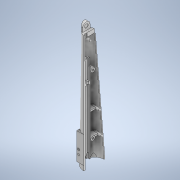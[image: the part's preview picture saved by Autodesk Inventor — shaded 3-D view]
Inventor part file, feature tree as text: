
AUTODESK INVENTOR PART (.ipt)
format: ipt  version: 2021 (Build 250183000, 183)  size: 1,114,112 bytes
history: native  units: mm
features: sketch x40, extrude x37, plane x17, fillet x7, hole x3, thread x3, loft x2, revolve x2, other x1
ambient origin geometry x8: Origin, YZ Plane, XZ Plane, XY Plane, X Axis, Y Axis, Z Axis, Center Point
bodies: Body1 (feature_tree)
feature tree (112):
  other  "Sólido1"
  plane  "Plano de trabajo1"
  plane  "Plano de trabajo2"
  plane  "Plano de trabajo4"
  plane  "Plano de trabajo5"
  plane  "Plano de trabajo6"
  sketch  "Boceto1"  dims[d1=250.0mm d2=0.0mm d3=-80.0mm d4=-110.0mm]
  sketch  "Boceto2"  dims[d5=-140.0mm d7=-0.0mm d8=2.0mm]
  sketch  "Boceto3"  dims[d9=140.0mm d10=250.0mm]
  sketch  "Boceto4"  dims[d11=24.0mm d22=0.0mm d23=90.0deg d24=0.0mm d25=90.0deg]
  sketch  "Boceto6"  dims[d44=45.0mm d49=29.11157mm]
  sketch  "Boceto7"  dims[d50=29.11157mm d53=29.11157mm]
  loft  "Solevación1"
  fillet  "Empalme2"  [1 undecoded]
  extrude  "Extrusión1"  TaperAngle=0.0deg  [1 undecoded]
  fillet  "Empalme5"  Radius=2.0mm
  plane  "Plano de trabajo7"
  extrude  "Extrusión2"  Depth=250.0mm
  plane  "Plano de trabajo8"
  plane  "Plano de trabajo9"
  loft  "Solevación9"
  plane  "Plano de trabajo10"
  extrude  "Extrusión3"  Depth=29.11157mm
  plane  "Plano de trabajo11"
  revolve  "Revolución1"  [1 undecoded]
  revolve  "Revolución2"  [1 undecoded]
  extrude  "Extrusión4"  Depth=32.5mm
  plane  "Plano de trabajo12"
  extrude  "Extrusión5"  Depth=44.747934mm
  plane  "Plano de trabajo13"
  plane  "Plano de trabajo14"
  extrude  "Extrusión6"  Depth=42.747934mm
  extrude  "Extrusión7"  Depth=42.747934mm
  extrude  "Extrusión8"  Depth=13.0mm
  extrude  "Extrusión11"  Depth=7.75mm
  extrude  "Extrusión9"  Depth=7.75mm
  extrude  "Extrusión10"  Depth=16.0mm
  extrude  "Extrusión12"  Depth=12.0mm
  sketch  "Boceto30"  dims[d160=-19.75mm d161=0.0mm]
  extrude  "Extrusión13"  Depth=7.75mm
  extrude  "Extrusión14"  Depth=7.75mm
  extrude  "Extrusión15"  TaperAngle=0.0deg  [1 undecoded]
  hole  "Agujero1"  [1 undecoded]
  thread  "Rosca1"  [1 undecoded]
  extrude  "Extrusión16"  Depth=2.0mm
  plane  "Plano de trabajo16"
  extrude  "Extrusión17"  TaperAngle=0.0deg  [1 undecoded]
  extrude  "Extrusión18"  TaperAngle=0.0deg  [1 undecoded]
  plane  "Plano de trabajo17"
  sketch  "Boceto46"  dims[d185=2.0mm d187=1.0mm]
  hole  "Agujero2"  [1 undecoded]
  hole  "Agujero3"  [1 undecoded]
  plane  "Plano de trabajo19"
  sketch  "Boceto50"  dims[d193=0.25mm d194=90.0deg d196=4.381635mm d197=0.0mm]
  extrude  "Extrusión22"  Depth=12.0mm
  extrude  "Extrusión23"  [1 undecoded]
  extrude  "Extrusión24"  Depth=0.75mm
  plane  "Plano de trabajo20"
  extrude  "Extrusión25"  Depth=1.0mm
  fillet  "Empalme6"  Radius=11.0mm
  fillet  "Empalme7"  Radius=17.453293mm
  sketch  "Boceto49"  dims[d191=2.0mm d192=0.25mm]
  extrude  "Extrusión29"  Depth=0.75mm
  extrude  "Extrusión30"  Depth=0.25mm
  sketch  "Boceto44"  dims[d181=0.75mm d182=0.25mm]
  sketch  "Boceto47"  dims[d189=3.0mm d190=2.0mm]
  extrude  "Extrusión26"  Depth=0.25mm
  extrude  "Extrusión27"  Depth=1.0mm
  extrude  "Extrusión28"  Depth=2.0mm
  sketch  "Boceto45"  dims[d183=1.0mm d184=0.25mm]
  extrude  "Extrusión31"  Depth=0.25mm
  extrude  "Extrusión32"  TaperAngle=90.0deg  [1 undecoded]
  fillet  "Empalme8"  Radius=4.381635mm
  extrude  "Extrusión33"  Depth=12.0mm
  extrude  "Extrusión34"  Depth=9.0mm
  thread  "Rosca2"  [1 undecoded]
  thread  "Rosca3"  [1 undecoded]
  fillet  "Empalme9"  Radius=201.65mm
  extrude  "Extrusión35"  Depth=0.5mm
  extrude  "Extrusión36"  [1 undecoded]
  sketch  "Boceto53"  dims[d205=0.0mm d206=0.5mm]
  extrude  "Agujero_tornillo_caja"  Depth=100.0mm TaperAngle=0.0deg
  extrude  "Extrusión39"  Depth=35.0mm TaperAngle=0.0deg
  extrude  "Test_section"  Depth=210.0mm TaperAngle=0.0deg
  extrude  "Agujero_cables"  Depth=2.0mm
  fillet  "Empalme10"  Radius=1.059493mm
  sketch  "Boceto9"  dims[d59=29.11157mm d61=29.11157mm]
  sketch  "Boceto10"  dims[d65=22.5mm d66=32.5mm]
  sketch  "Boceto15"  dims[d67=22.5mm d90=44.747934mm]
  sketch  "Boceto16"  dims[d91=42.747934mm d93=42.747934mm]
  sketch  "Boceto17"  dims[d96=0.0mm d97=90.0deg d98=0.0mm d99=90.0deg d100=0.0mm d101=90.0deg d102=0.0mm d103=90.0deg d112=42.747934mm]
  sketch  "Boceto18"  dims[d115=5.0mm d120=13.0mm]
  sketch  "Boceto19"  dims[d121=6.5mm d124=7.75mm]
  sketch  "Boceto20"  dims[d125=7.75mm d126=7.75mm]
  sketch  "Boceto21"  dims[d127=7.75mm d130=16.0mm]
  sketch  "Boceto22"  dims[d131=0.0mm d132=12.0mm]
  sketch  "Boceto24"  dims[d133=12.0mm d134=7.75mm]
  sketch  "Boceto25"  dims[d135=6.5mm d136=7.75mm]
  sketch  "Boceto26"  dims[d137=15.0mm d138=0.0mm]
  sketch  "Boceto27"  dims[d146=-8.5mm d147=30.0mm d148=2.0mm]
  sketch  "Boceto28"  dims[d149=25.12mm d150=2.0mm]
  sketch  "Boceto29"  dims[d151=10.357mm d156=0.0mm d157=90.0deg d158=0.0mm d159=90.0deg]
  sketch  "Boceto31"  dims[d163=0.0mm d164=2.0mm]
  sketch  "Boceto36"  dims[d165=15.0mm d166=4.0mm]
  sketch  "Boceto37"  dims[d167=30.0mm d168=12.0mm]
  sketch  "Boceto38"  dims[d169=0.0mm d170=-7.25mm]
  sketch  "Boceto39"  dims[d171=4.5mm d172=0.75mm]
  sketch  "Boceto40"  dims[d173=2.5mm d174=1.0mm d176=11.0mm d177=17.453293mm]
  sketch  "Boceto41"  dims[d179=2.939597mm d180=0.75mm]
  sketch  "Boceto51"  dims[d198=-48.35mm d199=12.0mm]
  sketch  "Boceto52"  dims[d200=20.0mm d201=9.0mm d202=9.0mm d203=2.0mm d204=201.65mm]
  sketch  "Boceto54"  dims[d207=0.25mm d208=-7.5mm d209=100.0mm d210=0.0mm d211=35.0mm d212=0.0mm d213=210.0mm d214=0.0mm d215=2.0mm d216=1.059493mm d217=6.5mm d218=1.059493mm d219=5.0mm d220=2.0mm d221=0.0mm d222=2.0mm d223=6.5mm d224=1.059493mm d225=5.0mm d226=4.85mm d227=2.0mm d228=0.0mm d229=6.0mm d230=10.0mm d231=3.0mm d232=11.0mm d233=10.5mm d235=30.0deg d236=4.75mm d237=0.0mm d238=-17.0mm d239=100.0mm d240=0.0mm d241=6.5mm d242=1.65mm d243=3.3mm d244=15.6mm d245=2.0mm d247=16.0mm d248=2.0mm d249=0.0mm d250=4.5mm d251=0.75mm d252=2.5mm d253=1.0mm d254=11.0mm d255=17.453293mm d256=2.939597mm d257=0.75mm d258=0.75mm d259=0.25mm d260=1.0mm d261=0.25mm d262=2.0mm d263=1.0mm d264=3.0mm d265=2.0mm d266=2.0mm d267=0.25mm d268=0.25mm d269=40.0mm d270=1.0mm d271=1.0mm d272=7.75mm d273=0.5mm d274=8.5mm d275=90.0deg d276=0.0mm d277=17.75mm d280=22.5mm d281=2.0mm d282=0.0mm d283=0.0mm d292=2.0mm d293=0.0mm d296=3.5mm d297=0.0mm d299=4.0mm d300=3.708mm d301=3.023mm d302=2.0mm d303=14.3117mm d304=16.0mm d305=0.0mm d306=16.0mm d307=0.0mm d314=6.0mm d315=19.2mm d316=6.0mm d317=19.2mm d318=13.0mm d320=6.0mm d321=19.2mm d322=13.0mm d323=6.0mm d324=19.2mm d325=13.0mm d326=7.0mm d332=10.0mm d333=0.0mm d335=-41.6mm d336=4.0mm d337=1.0mm d338=9.0mm d339=4.0mm d340=1.0mm d341=9.0mm d342=4.0mm d343=5.2mm d344=6.0mm d345=0.0mm d346=15.0mm d347=5.0mm d349=5.0mm d351=0.0mm d352=45.0mm d354=10.0mm d355=10.0mm d356=0.0mm d357=15.0mm d358=0.0mm d359=2.0mm d363=50.4125mm d376=14.059493mm d377=2.0mm d378=0.0mm d379=2.0mm d380=11.25mm d381=90.0mm d382=290.0mm d383=14.059493mm d384=100.825mm d390=30.940507mm d391=2.0mm d392=100.825mm d393=14.790546mm d394=2.0mm d395=3.0mm d396=4.0mm d397=4.0mm d398=4.0mm d399=4.0mm d400=8.128453mm d401=12.0mm d402=4.45mm d403=2.5mm d404=1.65mm d405=1.65mm d406=1.0mm d407=2.0mm d408=2.0mm d409=0.0mm d411=50.4125mm d412=4.0mm d418=13.059493mm d419=6.5mm d420=6.5mm d421=50.4125mm d422=126.03125mm d423=0.0mm d424=15.0mm d425=5.0mm d426=5.0mm d427=0.0mm d428=45.0mm d429=10.0mm d430=2.0mm d431=4.0mm d432=6.0mm d433=8.0mm d434=2.0mm d435=90.0deg d436=20.0mm d437=0.0mm d438=4.0mm d439=6.0mm d440=8.0mm d441=2.0mm d442=90.0deg d443=20.0mm d444=0.0mm d446=10.0mm d447=2.0mm d448=11.5mm d450=4.0mm d451=4.0mm d452=90.0mm d453=750.0mm d454=22.5mm d455=43.0mm d456=44.0mm d457=14.059493mm d458=11.25mm d461=22.5mm d462=43.0mm d463=7.059493mm d464=3.0mm d465=6.0mm d466=3.0mm d467=6.0mm d468=45.0mm d469=67.0mm d470=19.686mm d471=30.0mm d472=15.0mm d473=0.0mm d474=1.5mm d475=2.0mm d476=1.5mm d477=2.0mm d478=57.0mm d479=0.0mm d480=57.0mm d481=0.0mm d482=53.0mm d483=0.0mm d484=37.0mm d485=0.0mm d486=-1.5mm d487=33.895511mm d488=2.6mm d489=60.0deg d490=45.0deg d491=15.0mm d492=1.6mm d493=0.0mm d494=180.0mm d495=0.0mm d496=180.0mm d497=0.0mm d498=2.0mm d499=0.0mm d500=4.4mm d501=4.1mm d502=10.0mm d503=0.0mm d504=7.0mm d505=0.0mm d506=9.0mm d507=9.0mm d508=0.0mm d509=0.0mm d510=6.0mm d511=0.0mm d512=2.0mm d513=0.0mm d514=0.0mm d515=10.0mm d516=0.0mm d517=10.0mm d518=0.0mm d519=10.0mm d520=0.0mm d521=1.0mm d522=1.0mm d523=6.5mm d524=9.0mm d525=3.0mm d526=1.5mm d527=3.0mm d528=1.5mm d529=0.0mm d530=0.0mm d531=3.0mm d532=2.4mm d533=0.0mm d534=135.0mm d535=4.0mm d536=67.0mm d537=0.0mm d538=0.0mm d539=25.0mm d540=11.0mm d541=4.0mm d542=6.0mm d543=12.0mm d544=0.0mm d545=10.0mm d546=0.0mm d547=10.0mm d548=22.5mm d549=4.0mm d550=9.0mm d551=4.0mm d552=1.0mm d553=10.0mm d554=0.0mm d555=2.0mm]
note: 16 required parameter values undecoded (feature->parameter linkage not recoverable at this tier; creation-order binding heuristic only, values carry confidence <= 0.55)